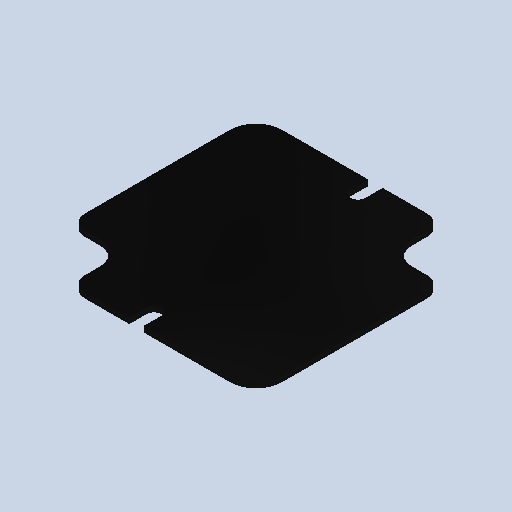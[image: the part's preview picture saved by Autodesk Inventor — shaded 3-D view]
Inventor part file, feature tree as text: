
AUTODESK INVENTOR PART (.ipt)
format: ipt  version: 2022.3 (Build 263350000, 350)  size: 75,264 bytes
history: native  units: mm (DEFAULTED — no unit token found)
features: fillet x1
ambient origin geometry x8: Origin, YZ Plane, XZ Plane, XY Plane, X Axis, Y Axis, Z Axis, Center Point
bodies: Solid1 (feature_tree)
feature tree (1):
  fillet  "Fillet2"  [1 undecoded]
note: 1 required parameter value undecoded (feature->parameter linkage not recoverable at this tier; creation-order binding heuristic only, values carry confidence <= 0.55)
